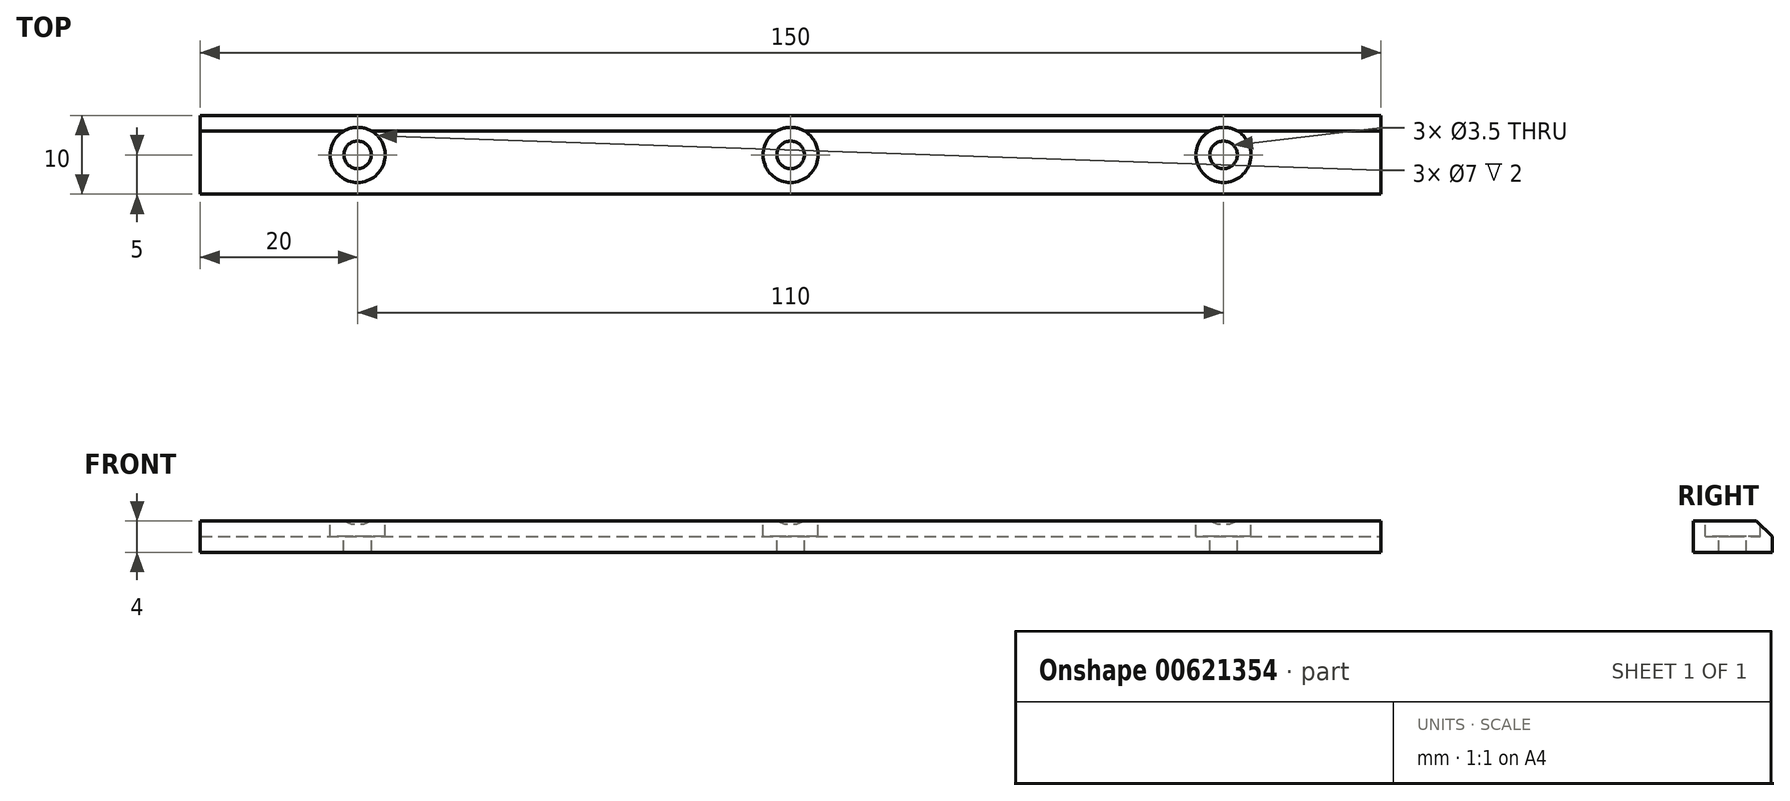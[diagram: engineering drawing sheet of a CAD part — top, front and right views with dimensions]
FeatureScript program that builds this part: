
annotation { "Feature Type Name" : "Feature", "Feature Type Description" : "" }
export const myFeature = defineFeature(function(context is Context, id is Id, definition is map)
    precondition{}
    {
        {
            var Q0;
            Q0=qCreatedBy(makeId("Top.planeOp"),FACE);
            var sketch = newSketch(context, id + "F0", { "sketchPlane" : qUnion([Q0])});
            skLineSegment(sketch, "E0", {"start": v(-75, 0) * mm, "end": v(75, 0) * mm});
            skLineSegment(sketch, "E1.0", {"start": v(-75, 10) * mm, "end": v(75, 10) * mm});
            skLineSegment(sketch, "E2", {"start": v(-75, 10) * mm, "end": v(-75, 0) * mm});
            skLineSegment(sketch, "E3", {"start": v(75, 10) * mm, "end": v(75, 0) * mm});
            skPoint(sketch, "E4", {"position": v(-55, 5) * mm});
            skPoint(sketch, "E5", {"position": v(0, 5) * mm});
            skPoint(sketch, "E6", {"position": v(55, 5) * mm});
            skSolve(sketch);
        }
        {
            var Q0;
            Q0=makeQuery(id+"F0.imprint","IMPRINT",FACE,{"disambiguationData":[TD([[makeQuery(id+"F0.imprint","IMPRINT",EDGE,{"derivedFrom":sQuery(id+"F0.wireOp",EDGE,"E0")}),1.0]])]});
            extrude(context, id + "F1", {"entities" : qUnion([Q0]), "oppositeDirection" : true, "depth" : 4 * mm, "offsetDistance" : 25 * mm});
        }
        {
            var Q0;
            Q0=sQuery(id+"F0.wireOp",VERTEX,"E4");
            var Q1;
            Q1=sQuery(id+"F0.wireOp",VERTEX,"E5");
            var Q2;
            Q2=sQuery(id+"F0.wireOp",VERTEX,"E6");
            var Q3;
            Q3=makeQuery(id+"F1.opExtrude","SWEPT_BODY",BODY,{"disambiguationData":[OSD([sQuery(id+"F0.wireOp",EDGE,"E0"),sQuery(id+"F0.wireOp",EDGE,"E1.0"),sQuery(id+"F0.wireOp",EDGE,"E2"),sQuery(id+"F0.wireOp",EDGE,"E3")])]});
            hole(context, id + "F2", {"style" : HoleStyle.C_BORE, "endStyle" : HoleEndStyle.THROUGH, "holeDiameter" : 3.5 * mm, "cBoreDiameter" : 7 * mm, "cBoreDepth" : 2 * mm, "majorDiameter" : 5 * mm, "isTappedThrough" : true, "tappedDepth" : 12 * mm, "tapClearance" : 3, "locations" : qUnion([Q0, Q1, Q2]), "scope" : qUnion([Q3])});
        }
        {
            var Q0;
            Q0=makeQuery(id+"F1.opExtrude","CAP_EDGE",EDGE,{"disambiguationData":[OSD([sQuery(id+"F0.wireOp",EDGE,"E1.0")])],"isStart":true});
            chamfer(context, id + "F3", {"entities" : qUnion([Q0]), "width" : 2 * mm, "tangentPropagation" : true});
        }
    });
